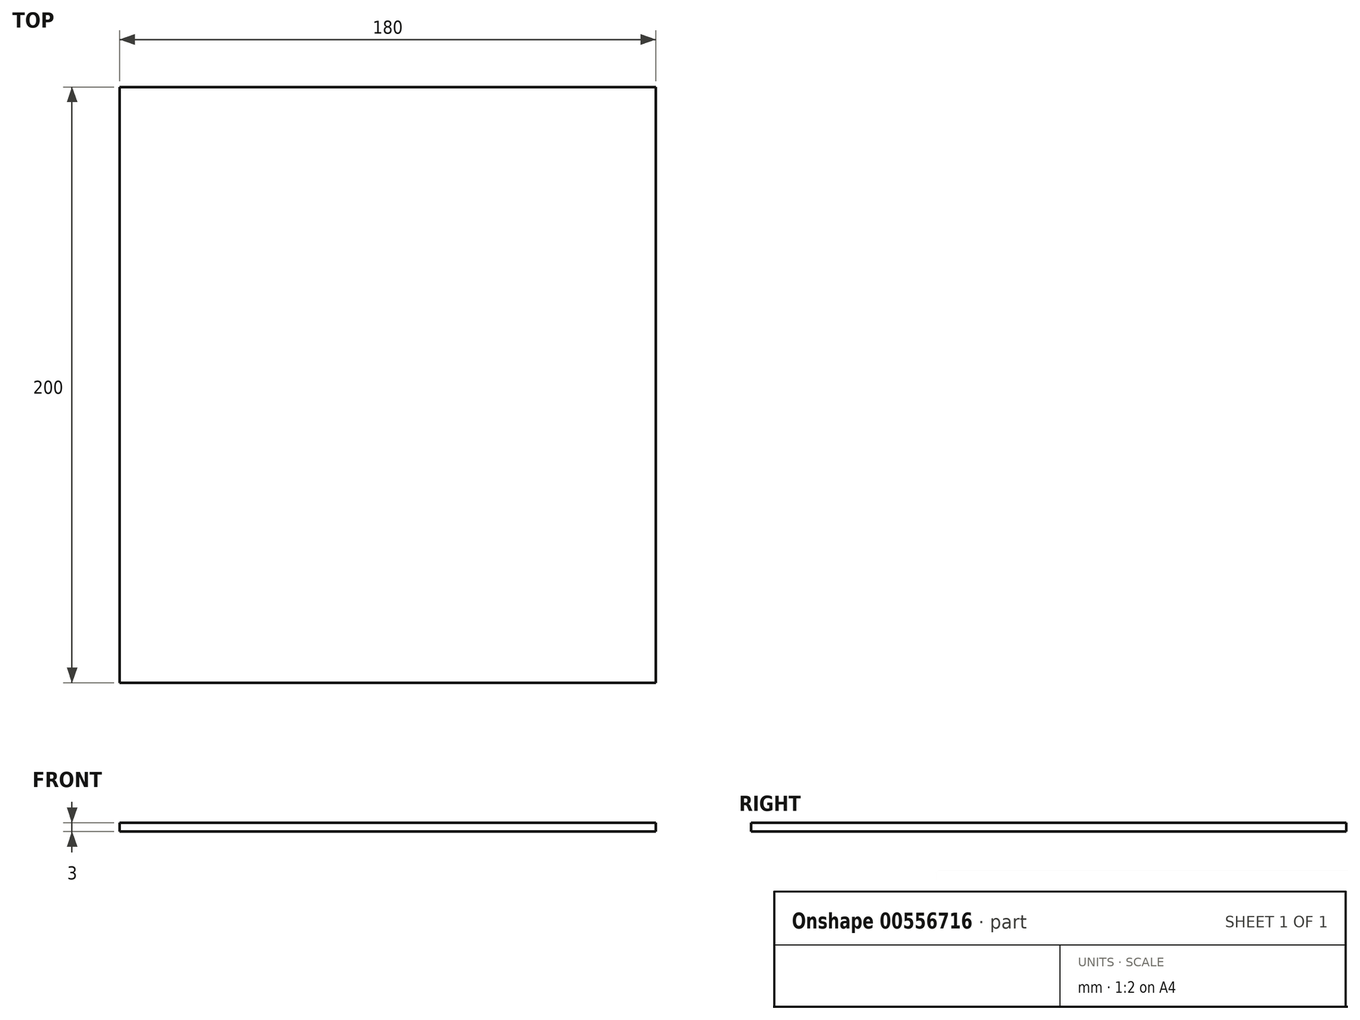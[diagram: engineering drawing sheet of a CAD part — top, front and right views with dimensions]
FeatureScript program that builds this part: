
annotation { "Feature Type Name" : "Feature", "Feature Type Description" : "" }
export const myFeature = defineFeature(function(context is Context, id is Id, definition is map)
    precondition{}
    {
        {
            var Q0;
            Q0=qCreatedBy(makeId("Top.planeOp"),FACE);
            var sketch = newSketch(context, id + "F0", { "sketchPlane" : qUnion([Q0])});
            skLineSegment(sketch, "E0", {"start": v(0, 0) * mm, "end": v(0, 200) * mm});
            skLineSegment(sketch, "E1", {"start": v(0, 200) * mm, "end": v(180, 200) * mm});
            skLineSegment(sketch, "E2", {"start": v(180, 200) * mm, "end": v(180, 0) * mm});
            skLineSegment(sketch, "E3", {"start": v(180, 0) * mm, "end": v(0, 0) * mm});
            skSolve(sketch);
        }
        {
            var Q0;
            Q0=makeQuery(id+"F0.imprint","IMPRINT",FACE,{"disambiguationData":[TD([[makeQuery(id+"F0.imprint","IMPRINT",EDGE,{"derivedFrom":sQuery(id+"F0.wireOp",EDGE,"E0")}),-1.0]])]});
            extrude(context, id + "F1", {"entities" : qUnion([Q0]), "depth" : 3 * mm, "offsetDistance" : 25 * mm, "symmetric" : true});
        }
    });
